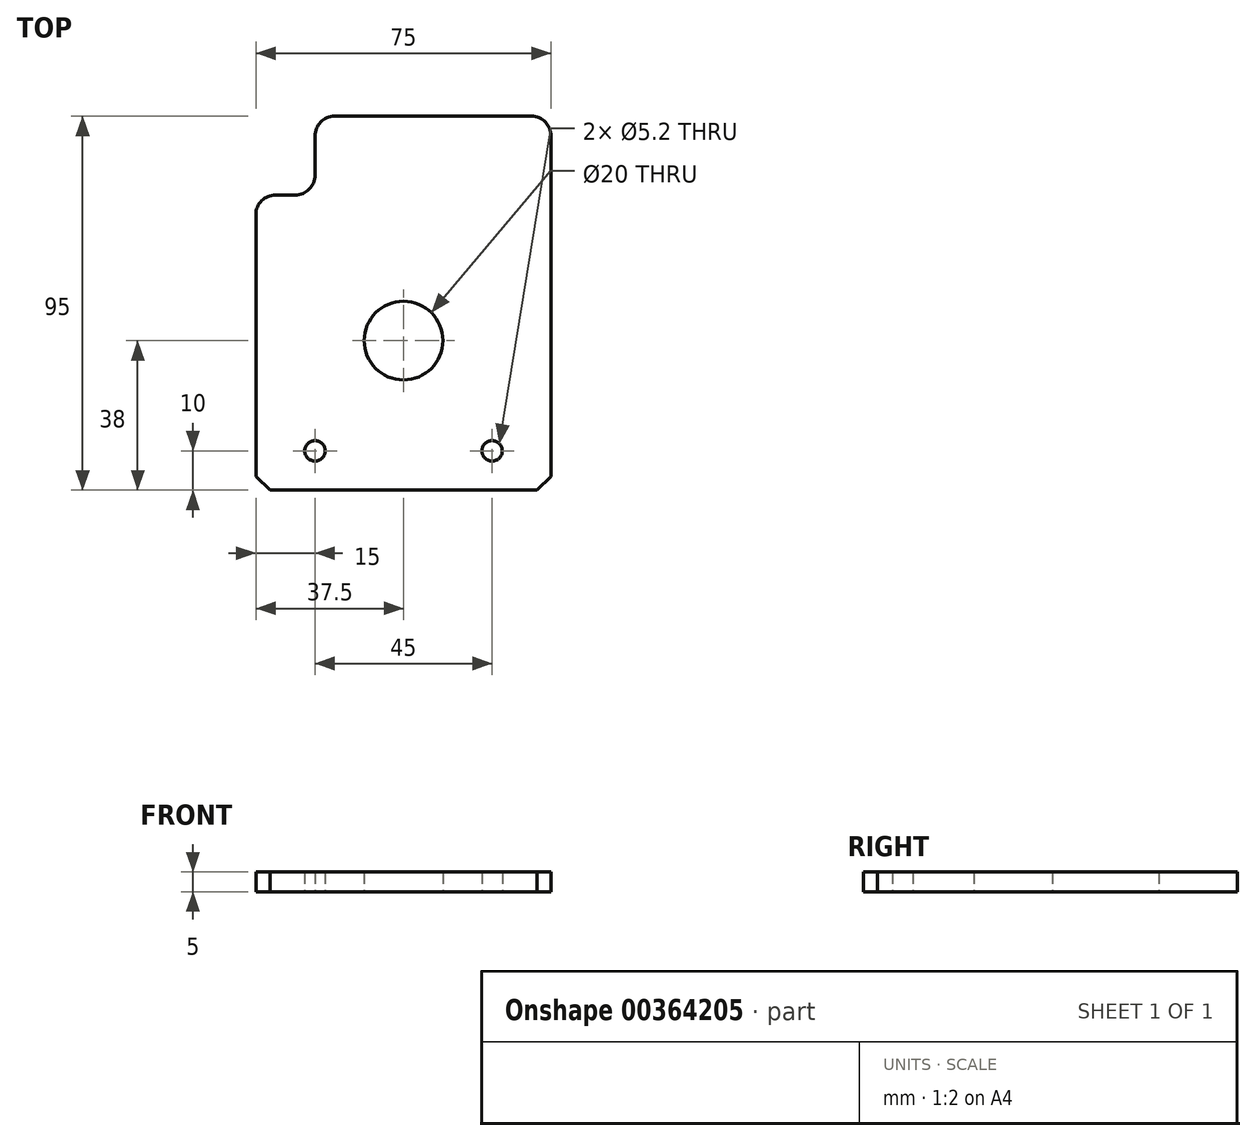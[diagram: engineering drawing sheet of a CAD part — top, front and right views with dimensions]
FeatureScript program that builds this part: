
annotation { "Feature Type Name" : "Feature", "Feature Type Description" : "" }
export const myFeature = defineFeature(function(context is Context, id is Id, definition is map)
    precondition{}
    {
        {
            var Q0;
            Q0=qCreatedBy(makeId("Top.planeOp"),FACE);
            var sketch = newSketch(context, id + "F0", { "sketchPlane" : qUnion([Q0])});
            skLineSegment(sketch, "E0.bottom", {"start": v(33.96, -47.5) * mm, "end": v(-33.96, -47.5) * mm});
            skLineSegment(sketch, "E0.top", {"start": v(32.5, 47.5) * mm, "end": v(-17.5, 47.5) * mm});
            skLineSegment(sketch, "E0.left", {"start": v(37.5, -43.96) * mm, "end": v(37.5, 42.5) * mm});
            skLineSegment(sketch, "E0.right", {"start": v(-37.5, -43.96) * mm, "end": v(-37.5, 22.5) * mm});
            skPoint(sketch, "E0.middle", {"position": v(0, 0) * mm});
            skLineSegment(sketch, "E1.top", {"start": v(-32.5, 27.5) * mm, "end": v(-27.5, 27.5) * mm});
            skLineSegment(sketch, "E1.right", {"start": v(-22.5, 42.5) * mm, "end": v(-22.5, 32.5) * mm});
            skPoint(sketch, "E2.orphan", {"position": v(-37.5, 47.5) * mm});
            skPoint(sketch, "E3.visualSharp", {"position": v(-22.5, 47.5) * mm});
            skArc(sketch, "E3.filletArc", {"start": v(-17.5, 47.5) * mm, "mid": v(-21.04, 46.04) * mm, "end": v(-22.5, 42.5) * mm});
            skPoint(sketch, "E4.visualSharp", {"position": v(-37.5, 27.5) * mm});
            skArc(sketch, "E4.filletArc", {"start": v(-32.5, 27.5) * mm, "mid": v(-36.04, 26.04) * mm, "end": v(-37.5, 22.5) * mm});
            skPoint(sketch, "E5.visualSharp", {"position": v(37.5, 47.5) * mm});
            skArc(sketch, "E5.filletArc", {"start": v(37.5, 42.5) * mm, "mid": v(36.04, 46.04) * mm, "end": v(32.5, 47.5) * mm});
            skLineSegment(sketch, "E6", {"start": v(37.5, -43.96) * mm, "end": v(33.96, -47.5) * mm});
            skLineSegment(sketch, "E7", {"start": v(-33.96, -47.5) * mm, "end": v(-37.5, -43.96) * mm});
            skPoint(sketch, "E8.orphan", {"position": v(37.5, -47.5) * mm});
            skPoint(sketch, "E9.orphan", {"position": v(-37.5, -47.5) * mm});
            skPoint(sketch, "E10.visualSharp", {"position": v(-22.5, 27.5) * mm});
            skArc(sketch, "E10.filletArc", {"start": v(-27.5, 27.5) * mm, "mid": v(-23.96, 28.96) * mm, "end": v(-22.5, 32.5) * mm});
            skCircle(sketch, "E11", {"center": v(0, -9.5) * mm, "radius": 10 * mm});
            skLineSegment(sketch, "E12", {"start": v(-37.5, -37.5) * mm, "end": v(37.5, -37.5) * mm, "construction": true});
            skCircle(sketch, "E13", {"center": v(-22.5, -37.5) * mm, "radius": 2.6 * mm});
            skCircle(sketch, "E14", {"center": v(22.5, -37.5) * mm, "radius": 2.6 * mm});
            skSolve(sketch);
        }
        {
            var Q0;
            Q0=makeQuery(id+"F0.imprint","IMPRINT",FACE,{"disambiguationData":[TD([[makeQuery(id+"F0.imprint","IMPRINT",EDGE,{"derivedFrom":sQuery(id+"F0.wireOp",EDGE,"E0.bottom")}),-1.0]])]});
            extrude(context, id + "F1", {"entities" : qUnion([Q0]), "depth" : 5 * mm, "offsetDistance" : 25 * mm});
        }
    });
